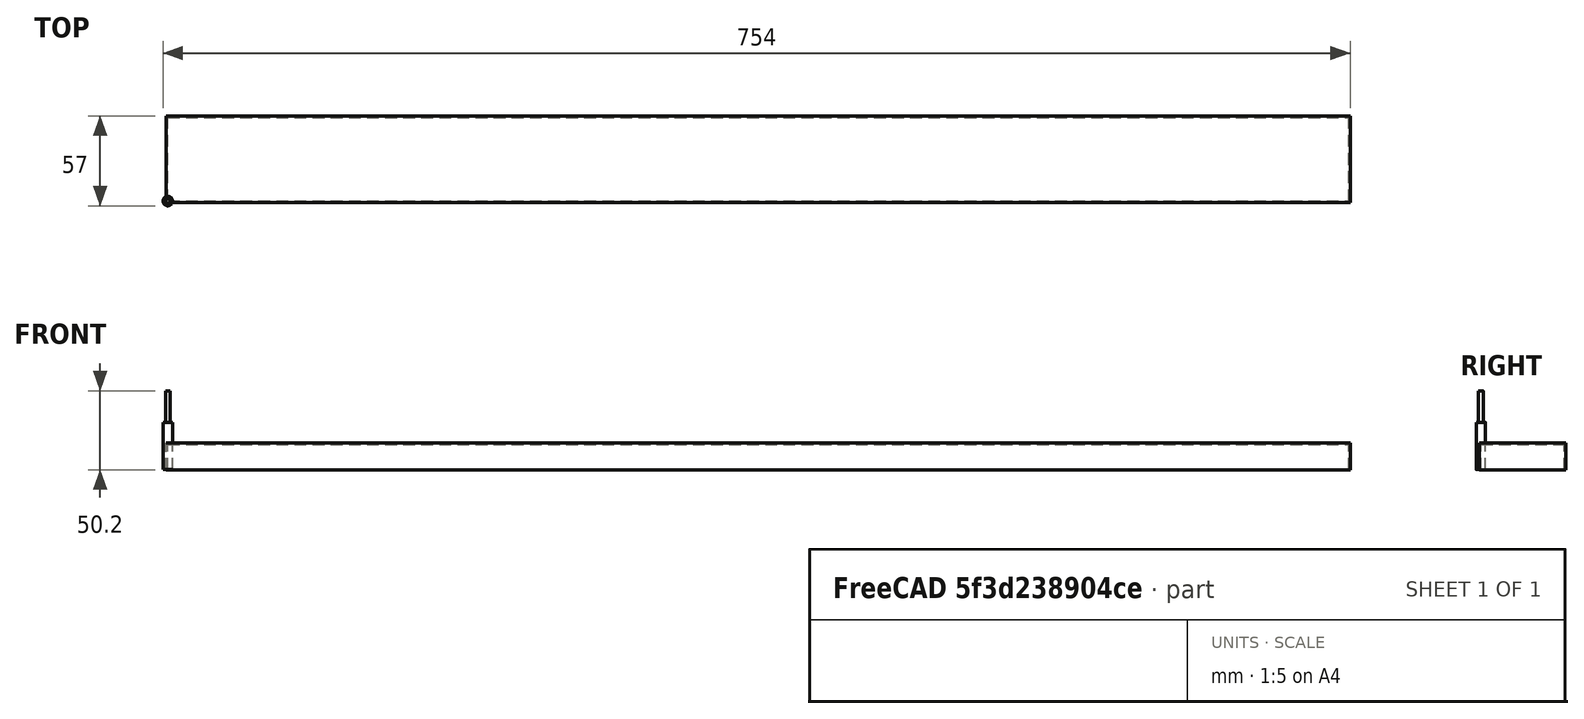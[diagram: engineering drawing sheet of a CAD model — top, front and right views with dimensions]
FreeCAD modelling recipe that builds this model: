
FCSTD DOCUMENT  (FreeCAD 0.20R29410 (Git))
Label: 53x750
License: All rights reserved
LicenseURL: http://en.wikipedia.org/wiki/All_rights_reserved
objects: Path::FeaturePython×4, Part::FeaturePython×3, App::DocumentObjectGroup×3, Part::Box×1, App::FeaturePython×1
note: 5 computed .brp shape members not serialized (recipe doc carries the construction recipe); baked Part::Feature solids carry a one-line shape summary decoded from their .brp

FEATURE [Part::Box] Box  label="Cube"
  AttacherType = Attacher::AttachEngine3D
  Height = 16
  Length = 750
  Width = 53
FEATURE [App::FeaturePython] SetupSheet  # Path/CAM operation (typed FeaturePython)
  ClearanceHeightExpression = OpStockZMax+SetupSheet.ClearanceHeightOffset
  ClearanceHeightOffset = 5
  CoolantMode = 0
  CoolantModes = None | Flood | Mist
  FinalDepthExpression = OpFinalDepth
  HorizRapid = 0
  SafeHeightExpression = OpStockZMax+SetupSheet.SafeHeightOffset
  SafeHeightOffset = 3
  StartDepthExpression = OpStartDepth
  StepDownExpression = OpToolDiameter
  VertRapid = 0
FEATURE [Part::FeaturePython] Clone  label="Model-Cube"  # Draft clone (typed FeaturePython)
  AttacherType = Attacher::AttachEngine3D
  Fuse = false
  Objects = -> [Box]
  PathResource = Model
  Scale = (1,1,1)
FEATURE [App::DocumentObjectGroup] Model
  Group = -> [Clone]
FEATURE [Part::FeaturePython] Stock  # WARN: FeaturePython — macro-defined, semantics opaque (R4)
  Base = -> Model
  ExtXneg = 1
  ExtXpos = 1
  ExtYneg = 1
  ExtYpos = 1
  ExtZneg = 0.2
  ExtZpos = 1
  StockType = FromBase
FEATURE [Part::FeaturePython] ToolBit001  label="6mm Endmill"  # Path/CAM toolbit (typed FeaturePython)
  BitPropertyNames = Chipload | CuttingEdgeHeight | Diameter | Flutes | Length | Material | ShankDiameter | SpindleDirection
  BitShape = <path>
  Chipload = 0
  CuttingEdgeHeight = 30
  Diameter = 6
  File = <userpath>/.local/share/FreeCAD/Macro/Bit/6mm_Endmill.fctb
  Flutes = 0
  Length = 50
  Material = 0
  ShankDiameter = 3
  ShapeName = endmill
  SpindleDirection = 0
FEATURE [Path::FeaturePython] _mm_Endmill  label="6mm Endmill001"  # Path/CAM operation (typed FeaturePython)
  HorizFeed = 51.6667
  HorizRapid = 0
  SpindleDir = 0
  SpindleSpeed = 18000
  Tool = -> ToolBit001
  ToolNumber = 2
  VertFeed = 16.6667
  VertRapid = 0
  expr: HorizRapid = SetupSheet.HorizRapid
  expr: VertRapid = SetupSheet.VertRapid
FEATURE [App::DocumentObjectGroup] Tools
  Group = -> [_mm_Endmill]
FEATURE [Path::FeaturePython] Profile  # Path/CAM operation (typed FeaturePython)
  Active = true
  AreaParams:
    Tolerance = 1e-07
    FitArcs = True
    Simplify = False
    CleanDistance = 0.0
    Accuracy = 0.01
    Unit = 1.0
    MinArcPoints = 4
    MaxArcPoints = 100
    ClipperScale = 10000000.0
    Fill = 0
    Coplanar = 0
    Reorient = True
    Outline = False
    Explode = False
    OpenMode = 0
    Deflection = 0.01
    SubjectFill = 0
    ClipFill = 0
    Offset = 3.0
    ExtraPass = 0
    Stepover = 0.0
    LastStepover = 0.0
    JoinType = 0
    EndType = 0
    MiterLimit = 2.0
    RoundPrecision = 0.0
    PocketMode = 0
    ToolRadius = 1.0
    PocketExtraOffset = 0.0
    PocketStepover = 0.0
    PocketLastStepover = 0.0
    FromCenter = False
    Angle = 45.0
    AngleShift = 0.0
    Shift = 0.0
    Thicken = False
    SectionCount = -1
    Stepdown = 1.0
    SectionOffset = 0.0
    SectionTolerance = 1e-06
    SectionMode = 2
    Project = False
  ClearanceHeight = 22
  CoolantMode = 0
  CycleTime = 00:01:52
  Direction = 0
  FinalDepth = -0.2
  HandleMultipleFeatures = 0
  JoinType = 0
  MiterLimit = 0.1
  OffsetExtra = 0
  OpFinalDepth = -0.2
  OpStartDepth = 17
  OpStockZMax = 17
  OpStockZMin = -0.2
  OpToolDiameter = 6
  PathParams = {'orientation': 1, 'feedrate': 51.666666666666664, 'feedrate_v': 16.666666666666668, 'verbose': True, 'resume_height': 20.0, 'retraction': 22.0, 'return_end': True, 'preamble': False}
  SafeHeight = 20
  Side = 0
  SplitArcs = false
  StartDepth = 17
  StartPoint = (0,0,0)
  StepDown = 6
  ToolController = -> _mm_Endmill
  UseComp = true
  UseStartPoint = false
  processCircles = false
  processHoles = false
  processPerimeter = true
  expr: ClearanceHeight = OpStockZMax + SetupSheet.ClearanceHeightOffset
  expr: FinalDepth = OpFinalDepth
  expr: SafeHeight = OpStockZMax + SetupSheet.SafeHeightOffset
  expr: StartDepth = OpStartDepth
  expr: StepDown = OpToolDiameter
FEATURE [Path::FeaturePython] Array  # Path/CAM operation (typed FeaturePython)
  Active = true
  Angle = 0
  Base = -> [Profile]
  Centre = (0,0,0)
  Copies = 1
  CopiesX = 0
  CopiesY = 0
  JitterMagnitude = (0,0,0)
  JitterPercent = 0
  JitterSeed = 0
  Offset = (0,59,0)
  SwapDirection = false
  ToolController = -> _mm_Endmill
  Type = 0
FEATURE [App::DocumentObjectGroup] Operations
  Group = -> [Profile,Array]
FEATURE [Path::FeaturePython] Job  # Path/CAM operation (typed FeaturePython)
  CycleTime = 00:01:52
  Fixtures = G54
  GeometryTolerance = 0.01
  JobType = 0
  LastPostProcessDate = 2022-12-23 17:04:49.184273
  LastPostProcessOutput = <userpath>/B653-DC8A/53x750.Job.tap
  Model = -> Model
  Operations = -> Operations
  OrderOutputBy = 0
  PostProcessor = 11
  PostProcessorOutputFile = %d.%j.tap
  SetupSheet = -> SetupSheet
  SplitOutput = false
  Stock = -> Stock
  Tools = -> Tools
note: 1 file-system path scrubbed to <path> (originals preserved in the JSON sidecar)
